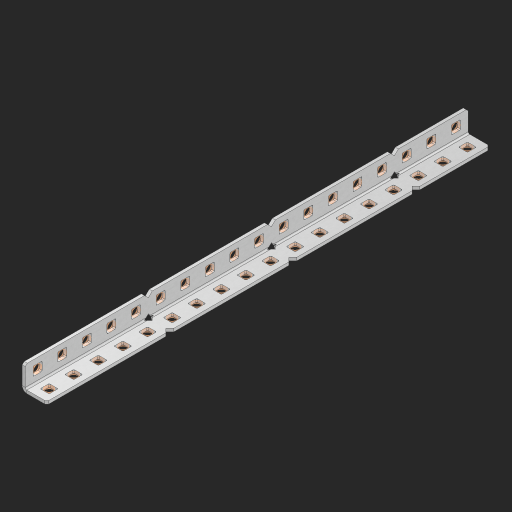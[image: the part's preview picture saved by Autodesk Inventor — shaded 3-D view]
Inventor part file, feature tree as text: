
AUTODESK INVENTOR PART (.ipt)
format: ipt  version: 2023 (Build 270158000, 158)  size: 766,464 bytes
history: native  units: in
note: dims shown in document units (in); Inventor stores cm internally (conversion verified against a paired STEP export)
features: other x42, extrude x37, sheet_metal_op x8, sketch x5, pattern_linear x1, mirror x1, chamfer x1
ambient origin geometry x8: Origin, YZ Plane, XZ Plane, XY Plane, X Axis, Y Axis, Z Axis, Center Point
bodies: Solid1 (feature_tree), Body (feature_tree)
feature tree (95):
  sheet_metal_op  "Flanges"
  sheet_metal_op  "Body Pattern"
  other  "Arc Length"
  pattern_linear  "Notch Pattern"  Spacing1=0.125in  [1 undecoded]
  other  "Diagonal Plane"
  mirror  "Everything Mirrored"
  chamfer  "End Chamfer"
  sketch  "Sketch1"  dims[d0=0.5in]
  other  "Plate1"
  sketch  "Sketch2"  dims[d1=9.0in]
  other  "Plate2"
  sheet_metal_op  "Bend1"
  sheet_metal_op  "Corner1"
  sketch  "Sketch8"  dims[d2=0.0625in]
  sketch  "Sketch9"  dims[d3=0.0625in]
  other  "Srf91"
  sheet_metal_op  "Body Pattern Sketch"
  other  "Srf92"
  sketch  "Sketch13"  dims[d4=0.0312in d5=0.125in d6=0.0625in d7=0.5in d8=90.0deg d9=0.0312in d10=0.25in d11=0.0625in d12=0.0625in d49=0.182in d50=0.02in d52=0.25in d53=0.0625in d54=0.0in d55=0.172in d56=1.0in d57=0.0in d85=0.1473in d86=0.1782in d89=0.0625in d90=0.0in d91=0.04in d92=0.0491in d95=2.5in d96=0.04in d97=0.25in d98=45.0deg d123=0.204in d126=0.0491in d127=0.1473in d128=0.08in d129=0.04in d130=2.5in d131=7.0866in d133=0.5in d134=0.3937in d136=1.0in]
  other  "Srf856"
  other  "Srf857"
  other  "Srf858"
  other  "Srf859"
  other  "Srf860"
  other  "Srf861"
  other  "Srf1275"
  other  "Srf1276"
  other  "Srf1278"
  other  "Srf1279"
  other  "Srf1280"
  other  "Srf1281"
  other  "Srf1282"
  other  "Srf1283"
  other  "Srf1383"
  other  "Srf1384"
  other  "Srf1385"
  other  "Srf1386"
  other  "Srf1387"
  other  "Srf1388"
  other  "Srf1389"
  other  "Srf1390"
  other  "Srf1391"
  other  "Srf1392"
  other  "Srf1393"
  other  "Srf1475"
  other  "Srf1476"
  other  "Srf1477"
  other  "Srf1478"
  other  "Srf1479"
  other  "Srf1480"
  other  "Srf1481"
  other  "Srf1482"
  other  "Srf1483"
  other  "Srf1484"
  other  "Srf1485"
  sheet_metal_op  "Body Stamp"
  sheet_metal_op  "Body Circle"
  sheet_metal_op  "Notch"
  extrude  "ExtrusionSrf92"  Depth=0.0625in
  extrude  "ExtrusionSrf856"  Depth=0.5in TaperAngle=90.0deg
  extrude  "ExtrusionSrf857"  Depth=0.25in
  extrude  "ExtrusionSrf858"  Depth=0.0625in
  extrude  "ExtrusionSrf859"  Depth=0.0625in
  extrude  "ExtrusionSrf860"  Depth=0.3937in
  extrude  "ExtrusionSrf861"  Depth=0.02in
  extrude  "ExtrusionSrf1275"  Depth=0.25in
  extrude  "ExtrusionSrf1276"  Depth=0.0625in
  extrude  "ExtrusionSrf1277"  TaperAngle=0.0deg  [1 undecoded]
  extrude  "ExtrusionSrf1278"  Depth=0.3937in
  extrude  "ExtrusionSrf1279"  Depth=0.3937in TaperAngle=0.0deg
  extrude  "ExtrusionSrf1280"  Depth=0.3937in
  extrude  "ExtrusionSrf1281"  Depth=0.3937in
  extrude  "ExtrusionSrf1282"  Depth=0.0625in
  extrude  "ExtrusionSrf1383"  Depth=0.3937in TaperAngle=0.0deg
  extrude  "ExtrusionSrf1384"  Depth=0.3937in
  extrude  "ExtrusionSrf1385"  Depth=0.25in TaperAngle=45.0deg
  extrude  "ExtrusionSrf1386"  Depth=0.3937in
  extrude  "ExtrusionSrf1387"  Depth=0.3937in
  extrude  "ExtrusionSrf1388"  Depth=0.3937in
  extrude  "ExtrusionSrf1389"  Depth=0.3937in
  extrude  "ExtrusionSrf1390"  Depth=0.3937in
  extrude  "ExtrusionSrf1391"  Depth=0.3937in
  extrude  "ExtrusionSrf1392"  Depth=0.3937in
  extrude  "ExtrusionSrf1393"  Depth=0.5in
  extrude  "ExtrusionSrf1475"  [1 undecoded]
  extrude  "ExtrusionSrf1476"  [1 undecoded]
  extrude  "ExtrusionSrf1477"  [1 undecoded]
  extrude  "ExtrusionSrf1478"  [1 undecoded]
  extrude  "ExtrusionSrf1479"  [1 undecoded]
  extrude  "ExtrusionSrf1480"  [1 undecoded]
  extrude  "ExtrusionSrf1481"  [1 undecoded]
  extrude  "ExtrusionSrf1482"  [1 undecoded]
  extrude  "ExtrusionSrf1483"  [1 undecoded]
  extrude  "ExtrusionSrf1484"  [1 undecoded]
  extrude  "ExtrusionSrf1485"  [1 undecoded]
note: 13 required parameter values undecoded (feature->parameter linkage not recoverable at this tier; creation-order binding heuristic only, values carry confidence <= 0.55)
